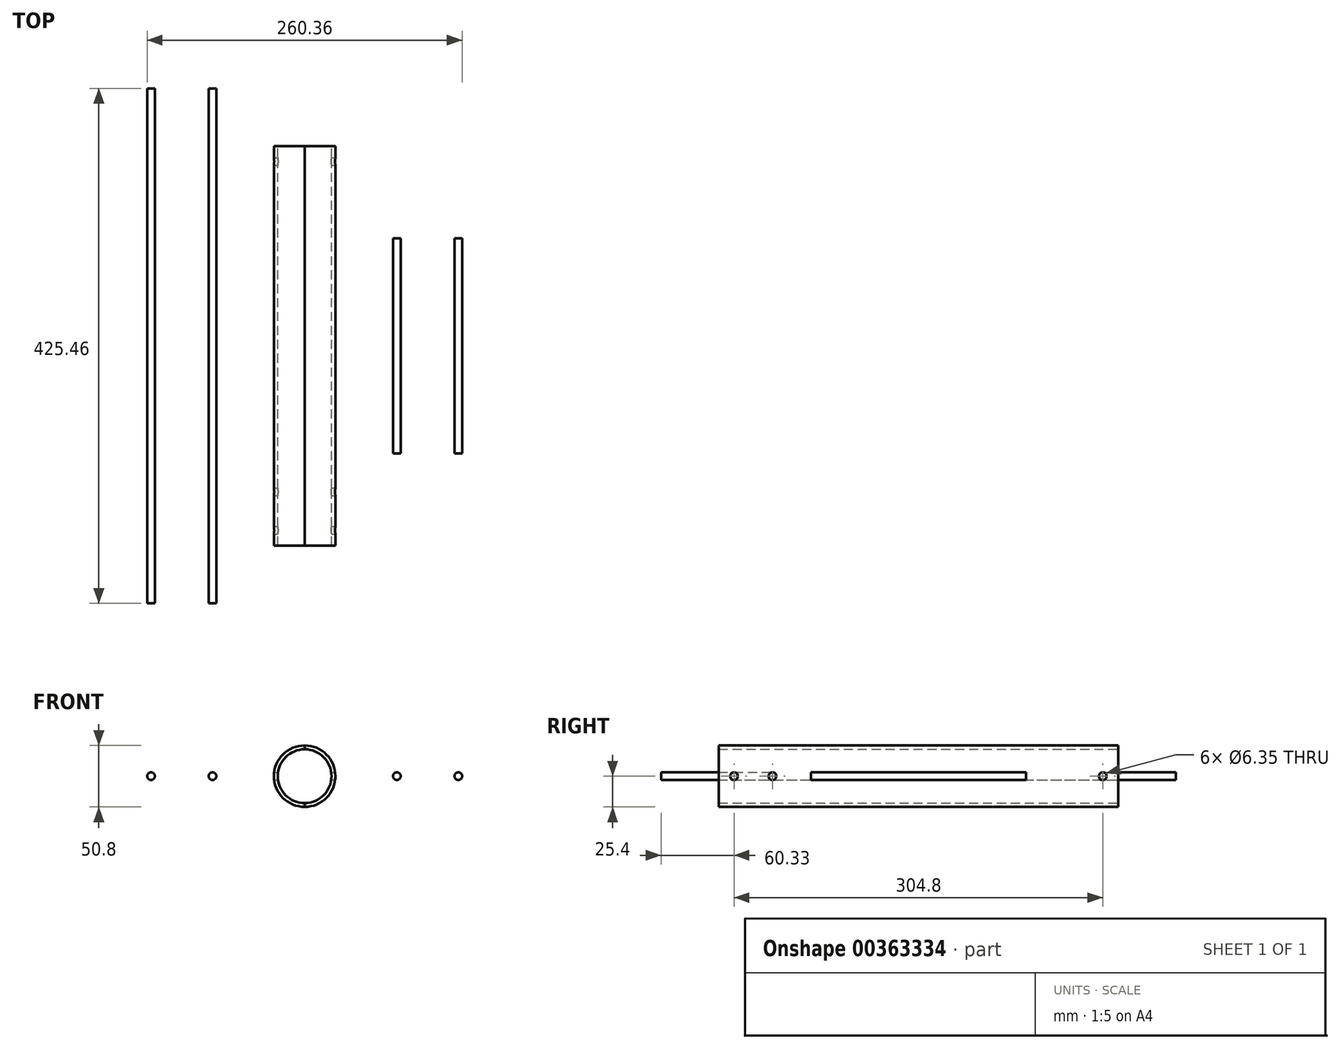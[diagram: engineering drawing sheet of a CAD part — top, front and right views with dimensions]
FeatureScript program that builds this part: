
annotation { "Feature Type Name" : "Feature", "Feature Type Description" : "" }
export const myFeature = defineFeature(function(context is Context, id is Id, definition is map)
    precondition{}
    {
        {
            var Q0;
            Q0=qCreatedBy(makeId("Front.planeOp"),FACE);
            var sketch = newSketch(context, id + "F0", { "sketchPlane" : qUnion([Q0])});
            skCircle(sketch, "E0", {"center": v(0, 0) * mm, "radius": 22.23 * mm});
            skCircle(sketch, "E1", {"center": v(0, 0) * mm, "radius": 25.4 * mm});
            skLineSegment(sketch, "E2", {"start": v(0, 25.4) * mm, "end": v(0, -25.4) * mm});
            skSolve(sketch);
        }
        {
            var Q0;
            {var subQ0=sQuery(id+"F0.wireOp",EDGE,"E2");var subQ1=sQuery(id+"F0.wireOp",EDGE,"E0");var subQ2=makeQuery(id+"F0.imprint","INTERSECT",VERTEX,{"disambiguationData":[OD(0.0)],"derivedFrom":[subQ1,subQ0]});Q0=makeQuery(id+"F0.imprint","IMPRINT",FACE,{"disambiguationData":[TD([[makeQuery(id+"F0.imprint","IMPRINT",EDGE,{"disambiguationData":[TD([[subQ2,-1.0]])],"derivedFrom":subQ1}),-1.0]])]});}
            extrude(context, id + "F1", {"entities" : qUnion([Q0]), "depth" : 330.2 * mm, "symmetric" : true});
        }
        {
            var Q0;
            {var subQ0=sQuery(id+"F0.wireOp",EDGE,"E2");var subQ1=sQuery(id+"F0.wireOp",EDGE,"E0");var subQ2=makeQuery(id+"F0.imprint","INTERSECT",VERTEX,{"disambiguationData":[OD(0.0)],"derivedFrom":[subQ1,subQ0]});Q0=makeQuery(id+"F0.imprint","IMPRINT",FACE,{"disambiguationData":[TD([[makeQuery(id+"F0.imprint","IMPRINT",EDGE,{"disambiguationData":[TD([[subQ2,1.0]])],"derivedFrom":subQ1}),-1.0]])]});}
            extrude(context, id + "F2", {"entities" : qUnion([Q0]), "depth" : 330.2 * mm, "symmetric" : true});
        }
        {
            var Q0;
            Q0=qCreatedBy(makeId("Front.planeOp"),FACE);
            var sketch = newSketch(context, id + "F3", { "sketchPlane" : qUnion([Q0])});
            skLineSegment(sketch, "E3", {"start": v(-127, 0) * mm, "end": v(127, 0) * mm, "construction": true});
            skLineSegment(sketch, "E4", {"start": v(0, -127) * mm, "end": v(0, 127) * mm, "construction": true});
            skCircle(sketch, "E5", {"center": v(127, 0) * mm, "radius": 3.18 * mm});
            skCircle(sketch, "E6", {"center": v(-127, 0) * mm, "radius": 3.18 * mm});
            skCircle(sketch, "E7", {"center": v(76.2, 0) * mm, "radius": 3.18 * mm});
            skCircle(sketch, "E8", {"center": v(-76.2, 0) * mm, "radius": 3.18 * mm});
            skLineSegment(sketch, "E9", {"start": v(76.2, 0) * mm, "end": v(127, 0) * mm, "construction": true});
            skPoint(sketch, "E10", {"position": v(101.6, 0) * mm});
            skSolve(sketch);
        }
        {
            var Q0;
            Q0=qCreatedBy(makeId("Right.planeOp"),FACE);
            var sketch = newSketch(context, id + "F4", { "sketchPlane" : qUnion([Q0])});
            skLineSegment(sketch, "E11", {"start": v(-152.4, 0) * mm, "end": v(152.4, 0) * mm, "construction": true});
            skCircle(sketch, "E12", {"center": v(-152.4, 0) * mm, "radius": 3.18 * mm});
            skCircle(sketch, "E13", {"center": v(152.4, 0) * mm, "radius": 3.18 * mm});
            skCircle(sketch, "E14", {"center": v(-120.65, 0) * mm, "radius": 3.18 * mm});
            skLineSegment(sketch, "E15", {"start": v(0, 0) * mm, "end": v(-152.4, 0) * mm, "construction": true});
            skSolve(sketch);
        }
        {
            var Q0;
            Q0 = qSketchRegion(id + "F4", true);
            var Q1;
            Q1 = qConstructionFilter(qBodyType(qCreatedBy(id + "F4" ,EDGE), BodyType.WIRE), ConstructionObject.NO);
            extrude(context, id + "F5", {"entities" : qUnion([Q0]), "operationType" : NewBodyOperationType.REMOVE, "surfaceEntities" : qUnion([Q1]), "endBound" : BoundingType.THROUGH_ALL, "oppositeDirection" : true, "depth" : 25.4 * mm, "hasSecondDirection" : true, "secondDirectionBound" : BoundingType.THROUGH_ALL, "secondDirectionOppositeDirection" : false, "secondDirectionDepth" : 25.4 * mm});
        }
        {
            var Q0;
            Q0=makeQuery(id+"F3.imprint","IMPRINT",FACE,{"disambiguationData":[TD([[makeQuery(id+"F3.imprint","IMPRINT",EDGE,{"derivedFrom":sQuery(id+"F3.wireOp",EDGE,"E6")}),1.0]])]});
            var Q1;
            Q1=makeQuery(id+"F3.imprint","IMPRINT",FACE,{"disambiguationData":[TD([[makeQuery(id+"F3.imprint","IMPRINT",EDGE,{"derivedFrom":sQuery(id+"F3.wireOp",EDGE,"E8")}),1.0]])]});
            extrude(context, id + "F6", {"entities" : qUnion([Q0, Q1]), "depth" : 425.45 * mm, "symmetric" : true});
        }
        {
            var Q0;
            Q0=makeQuery(id+"F3.imprint","IMPRINT",FACE,{"disambiguationData":[TD([[makeQuery(id+"F3.imprint","IMPRINT",EDGE,{"derivedFrom":sQuery(id+"F3.wireOp",EDGE,"E7")}),1.0]])]});
            var Q1;
            Q1=makeQuery(id+"F3.imprint","IMPRINT",FACE,{"disambiguationData":[TD([[makeQuery(id+"F3.imprint","IMPRINT",EDGE,{"derivedFrom":sQuery(id+"F3.wireOp",EDGE,"E5")}),1.0]])]});
            extrude(context, id + "F7", {"entities" : qUnion([Q0, Q1]), "depth" : 177.8 * mm, "symmetric" : true});
        }
    });
